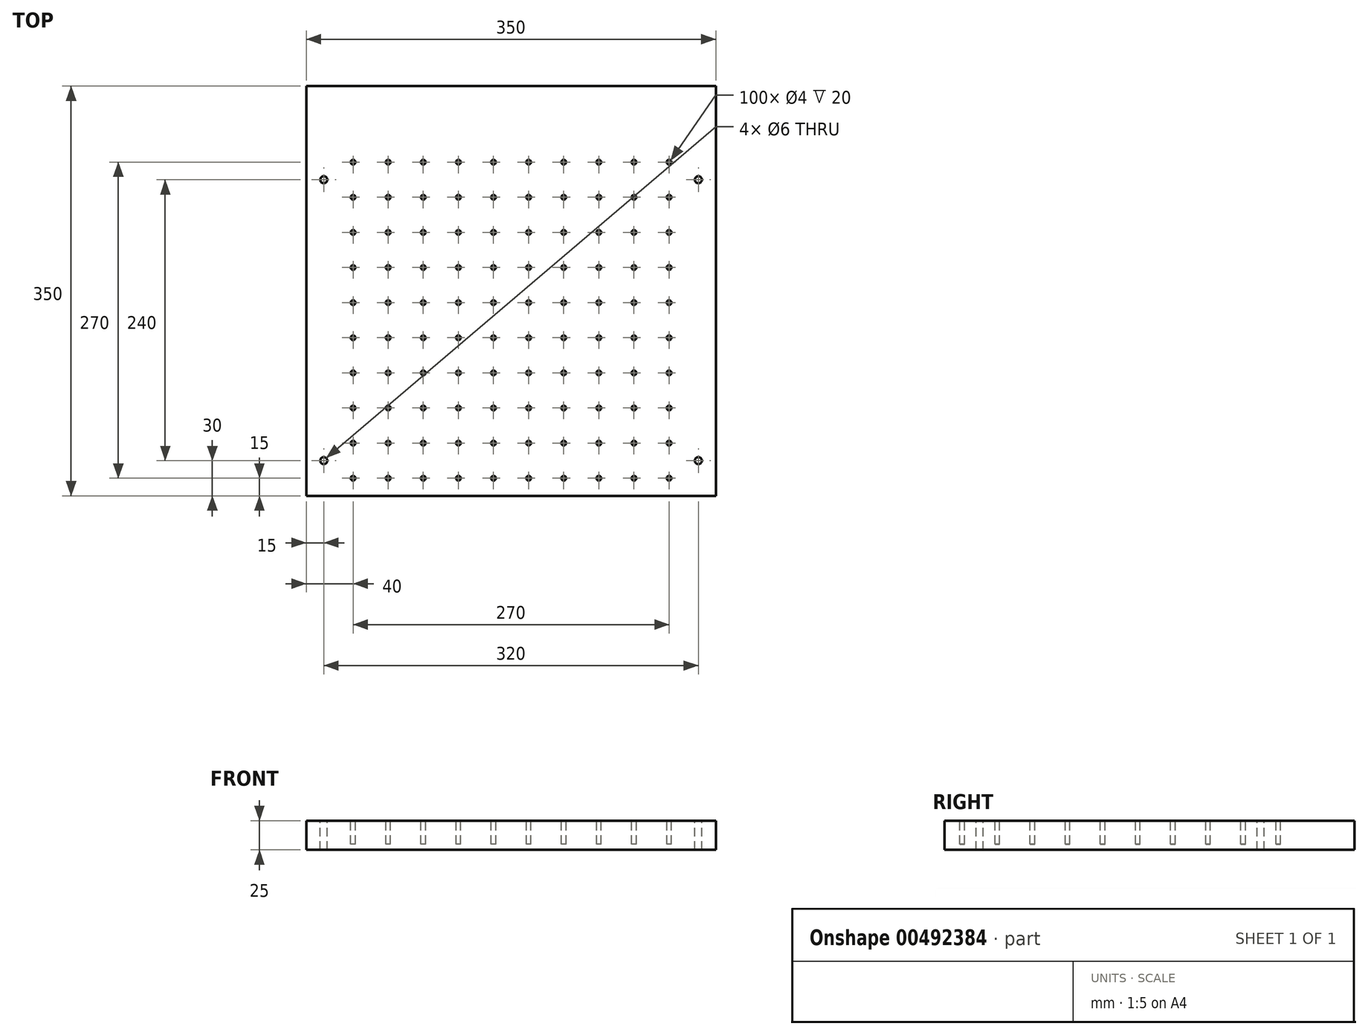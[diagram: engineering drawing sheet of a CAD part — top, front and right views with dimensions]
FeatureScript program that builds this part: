
annotation { "Feature Type Name" : "Feature", "Feature Type Description" : "" }
export const myFeature = defineFeature(function(context is Context, id is Id, definition is map)
    precondition{}
    {
        {
            var Q0;
            Q0=qCreatedBy(makeId("Top.planeOp"),FACE);
            var sketch = newSketch(context, id + "F0", { "sketchPlane" : qUnion([Q0])});
            skLineSegment(sketch, "E0.bottom", {"start": v(0, 0) * mm, "end": v(350, 0) * mm});
            skLineSegment(sketch, "E0.top", {"start": v(0, 300) * mm, "end": v(350, 300) * mm});
            skLineSegment(sketch, "E0.left", {"start": v(0, 0) * mm, "end": v(0, 300) * mm});
            skLineSegment(sketch, "E0.right", {"start": v(350, 0) * mm, "end": v(350, 300) * mm});
            skLineSegment(sketch, "E1.top", {"start": v(0, 350) * mm, "end": v(350, 350) * mm});
            skLineSegment(sketch, "E1.left", {"start": v(0, 300) * mm, "end": v(0, 350) * mm});
            skLineSegment(sketch, "E1.right", {"start": v(350, 300) * mm, "end": v(350, 350) * mm});
            skSolve(sketch);
        }
        {
            var Q0;
            Q0 = qSketchRegion(id + "F0", true);
            extrude(context, id + "F1", {"entities" : qUnion([Q0]), "depth" : 25 * mm});
        }
        {
            var Q0;
            Q0=makeQuery(id+"F1.opExtrude","CAP_FACE",FACE,{"disambiguationData":[OSD([sQuery(id+"F0.wireOp",EDGE,"E0.bottom"),sQuery(id+"F0.wireOp",EDGE,"E0.top"),sQuery(id+"F0.wireOp",EDGE,"E0.left"),sQuery(id+"F0.wireOp",EDGE,"E0.right")])],"isStart":false});
            var sketch = newSketch(context, id + "F2", { "sketchPlane" : qUnion([Q0])});
            skCircle(sketch, "E2", {"center": v(40, 15) * mm, "radius": 2 * mm});
            skCircle(sketch, "E3.0.1.0", {"center": v(40, 45) * mm, "radius": 2 * mm});
            skCircle(sketch, "E3.0.2.0", {"center": v(40, 75) * mm, "radius": 2 * mm});
            skCircle(sketch, "E3.0.3.0", {"center": v(40, 105) * mm, "radius": 2 * mm});
            skCircle(sketch, "E3.0.4.0", {"center": v(40, 135) * mm, "radius": 2 * mm});
            skCircle(sketch, "E3.0.5.0", {"center": v(40, 165) * mm, "radius": 2 * mm});
            skCircle(sketch, "E3.0.6.0", {"center": v(40, 195) * mm, "radius": 2 * mm});
            skCircle(sketch, "E3.0.7.0", {"center": v(40, 225) * mm, "radius": 2 * mm});
            skCircle(sketch, "E3.0.8.0", {"center": v(40, 255) * mm, "radius": 2 * mm});
            skCircle(sketch, "E3.0.9.0", {"center": v(40, 285) * mm, "radius": 2 * mm});
            skCircle(sketch, "E3.1.0.0", {"center": v(70, 15) * mm, "radius": 2 * mm});
            skCircle(sketch, "E3.1.1.0", {"center": v(70, 45) * mm, "radius": 2 * mm});
            skCircle(sketch, "E3.1.2.0", {"center": v(70, 75) * mm, "radius": 2 * mm});
            skCircle(sketch, "E3.1.3.0", {"center": v(70, 105) * mm, "radius": 2 * mm});
            skCircle(sketch, "E3.1.4.0", {"center": v(70, 135) * mm, "radius": 2 * mm});
            skCircle(sketch, "E3.1.5.0", {"center": v(70, 165) * mm, "radius": 2 * mm});
            skCircle(sketch, "E3.1.6.0", {"center": v(70, 195) * mm, "radius": 2 * mm});
            skCircle(sketch, "E3.1.7.0", {"center": v(70, 225) * mm, "radius": 2 * mm});
            skCircle(sketch, "E3.1.8.0", {"center": v(70, 255) * mm, "radius": 2 * mm});
            skCircle(sketch, "E3.1.9.0", {"center": v(70, 285) * mm, "radius": 2 * mm});
            skCircle(sketch, "E3.2.0.0", {"center": v(100, 15) * mm, "radius": 2 * mm});
            skCircle(sketch, "E3.2.1.0", {"center": v(100, 45) * mm, "radius": 2 * mm});
            skCircle(sketch, "E3.2.2.0", {"center": v(100, 75) * mm, "radius": 2 * mm});
            skCircle(sketch, "E3.2.3.0", {"center": v(100, 105) * mm, "radius": 2 * mm});
            skCircle(sketch, "E3.2.4.0", {"center": v(100, 135) * mm, "radius": 2 * mm});
            skCircle(sketch, "E3.2.5.0", {"center": v(100, 165) * mm, "radius": 2 * mm});
            skCircle(sketch, "E3.2.6.0", {"center": v(100, 195) * mm, "radius": 2 * mm});
            skCircle(sketch, "E3.2.7.0", {"center": v(100, 225) * mm, "radius": 2 * mm});
            skCircle(sketch, "E3.2.8.0", {"center": v(100, 255) * mm, "radius": 2 * mm});
            skCircle(sketch, "E3.2.9.0", {"center": v(100, 285) * mm, "radius": 2 * mm});
            skCircle(sketch, "E3.3.0.0", {"center": v(130, 15) * mm, "radius": 2 * mm});
            skCircle(sketch, "E3.3.1.0", {"center": v(130, 45) * mm, "radius": 2 * mm});
            skCircle(sketch, "E3.3.2.0", {"center": v(130, 75) * mm, "radius": 2 * mm});
            skCircle(sketch, "E3.3.3.0", {"center": v(130, 105) * mm, "radius": 2 * mm});
            skCircle(sketch, "E3.3.4.0", {"center": v(130, 135) * mm, "radius": 2 * mm});
            skCircle(sketch, "E3.3.5.0", {"center": v(130, 165) * mm, "radius": 2 * mm});
            skCircle(sketch, "E3.3.6.0", {"center": v(130, 195) * mm, "radius": 2 * mm});
            skCircle(sketch, "E3.3.7.0", {"center": v(130, 225) * mm, "radius": 2 * mm});
            skCircle(sketch, "E3.3.8.0", {"center": v(130, 255) * mm, "radius": 2 * mm});
            skCircle(sketch, "E3.3.9.0", {"center": v(130, 285) * mm, "radius": 2 * mm});
            skCircle(sketch, "E3.4.0.0", {"center": v(160, 15) * mm, "radius": 2 * mm});
            skCircle(sketch, "E3.4.1.0", {"center": v(160, 45) * mm, "radius": 2 * mm});
            skCircle(sketch, "E3.4.2.0", {"center": v(160, 75) * mm, "radius": 2 * mm});
            skCircle(sketch, "E3.4.3.0", {"center": v(160, 105) * mm, "radius": 2 * mm});
            skCircle(sketch, "E3.4.4.0", {"center": v(160, 135) * mm, "radius": 2 * mm});
            skCircle(sketch, "E3.4.5.0", {"center": v(160, 165) * mm, "radius": 2 * mm});
            skCircle(sketch, "E3.4.6.0", {"center": v(160, 195) * mm, "radius": 2 * mm});
            skCircle(sketch, "E3.4.7.0", {"center": v(160, 225) * mm, "radius": 2 * mm});
            skCircle(sketch, "E3.4.8.0", {"center": v(160, 255) * mm, "radius": 2 * mm});
            skCircle(sketch, "E3.4.9.0", {"center": v(160, 285) * mm, "radius": 2 * mm});
            skCircle(sketch, "E3.5.0.0", {"center": v(190, 15) * mm, "radius": 2 * mm});
            skCircle(sketch, "E3.5.1.0", {"center": v(190, 45) * mm, "radius": 2 * mm});
            skCircle(sketch, "E3.5.2.0", {"center": v(190, 75) * mm, "radius": 2 * mm});
            skCircle(sketch, "E3.5.3.0", {"center": v(190, 105) * mm, "radius": 2 * mm});
            skCircle(sketch, "E3.5.4.0", {"center": v(190, 135) * mm, "radius": 2 * mm});
            skCircle(sketch, "E3.5.5.0", {"center": v(190, 165) * mm, "radius": 2 * mm});
            skCircle(sketch, "E3.5.6.0", {"center": v(190, 195) * mm, "radius": 2 * mm});
            skCircle(sketch, "E3.5.7.0", {"center": v(190, 225) * mm, "radius": 2 * mm});
            skCircle(sketch, "E3.5.8.0", {"center": v(190, 255) * mm, "radius": 2 * mm});
            skCircle(sketch, "E3.5.9.0", {"center": v(190, 285) * mm, "radius": 2 * mm});
            skCircle(sketch, "E3.6.0.0", {"center": v(220, 15) * mm, "radius": 2 * mm});
            skCircle(sketch, "E3.6.1.0", {"center": v(220, 45) * mm, "radius": 2 * mm});
            skCircle(sketch, "E3.6.2.0", {"center": v(220, 75) * mm, "radius": 2 * mm});
            skCircle(sketch, "E3.6.3.0", {"center": v(220, 105) * mm, "radius": 2 * mm});
            skCircle(sketch, "E3.6.4.0", {"center": v(220, 135) * mm, "radius": 2 * mm});
            skCircle(sketch, "E3.6.5.0", {"center": v(220, 165) * mm, "radius": 2 * mm});
            skCircle(sketch, "E3.6.6.0", {"center": v(220, 195) * mm, "radius": 2 * mm});
            skCircle(sketch, "E3.6.7.0", {"center": v(220, 225) * mm, "radius": 2 * mm});
            skCircle(sketch, "E3.6.8.0", {"center": v(220, 255) * mm, "radius": 2 * mm});
            skCircle(sketch, "E3.6.9.0", {"center": v(220, 285) * mm, "radius": 2 * mm});
            skCircle(sketch, "E3.7.0.0", {"center": v(250, 15) * mm, "radius": 2 * mm});
            skCircle(sketch, "E3.7.1.0", {"center": v(250, 45) * mm, "radius": 2 * mm});
            skCircle(sketch, "E3.7.2.0", {"center": v(250, 75) * mm, "radius": 2 * mm});
            skCircle(sketch, "E3.7.3.0", {"center": v(250, 105) * mm, "radius": 2 * mm});
            skCircle(sketch, "E3.7.4.0", {"center": v(250, 135) * mm, "radius": 2 * mm});
            skCircle(sketch, "E3.7.5.0", {"center": v(250, 165) * mm, "radius": 2 * mm});
            skCircle(sketch, "E3.7.6.0", {"center": v(250, 195) * mm, "radius": 2 * mm});
            skCircle(sketch, "E3.7.7.0", {"center": v(250, 225) * mm, "radius": 2 * mm});
            skCircle(sketch, "E3.7.8.0", {"center": v(250, 255) * mm, "radius": 2 * mm});
            skCircle(sketch, "E3.7.9.0", {"center": v(250, 285) * mm, "radius": 2 * mm});
            skCircle(sketch, "E3.8.0.0", {"center": v(280, 15) * mm, "radius": 2 * mm});
            skCircle(sketch, "E3.8.1.0", {"center": v(280, 45) * mm, "radius": 2 * mm});
            skCircle(sketch, "E3.8.2.0", {"center": v(280, 75) * mm, "radius": 2 * mm});
            skCircle(sketch, "E3.8.3.0", {"center": v(280, 105) * mm, "radius": 2 * mm});
            skCircle(sketch, "E3.8.4.0", {"center": v(280, 135) * mm, "radius": 2 * mm});
            skCircle(sketch, "E3.8.5.0", {"center": v(280, 165) * mm, "radius": 2 * mm});
            skCircle(sketch, "E3.8.6.0", {"center": v(280, 195) * mm, "radius": 2 * mm});
            skCircle(sketch, "E3.8.7.0", {"center": v(280, 225) * mm, "radius": 2 * mm});
            skCircle(sketch, "E3.8.8.0", {"center": v(280, 255) * mm, "radius": 2 * mm});
            skCircle(sketch, "E3.8.9.0", {"center": v(280, 285) * mm, "radius": 2 * mm});
            skCircle(sketch, "E3.9.0.0", {"center": v(310, 15) * mm, "radius": 2 * mm});
            skCircle(sketch, "E3.9.1.0", {"center": v(310, 45) * mm, "radius": 2 * mm});
            skCircle(sketch, "E3.9.2.0", {"center": v(310, 75) * mm, "radius": 2 * mm});
            skCircle(sketch, "E3.9.3.0", {"center": v(310, 105) * mm, "radius": 2 * mm});
            skCircle(sketch, "E3.9.4.0", {"center": v(310, 135) * mm, "radius": 2 * mm});
            skCircle(sketch, "E3.9.5.0", {"center": v(310, 165) * mm, "radius": 2 * mm});
            skCircle(sketch, "E3.9.6.0", {"center": v(310, 195) * mm, "radius": 2 * mm});
            skCircle(sketch, "E3.9.7.0", {"center": v(310, 225) * mm, "radius": 2 * mm});
            skCircle(sketch, "E3.9.8.0", {"center": v(310, 255) * mm, "radius": 2 * mm});
            skCircle(sketch, "E3.9.9.0", {"center": v(310, 285) * mm, "radius": 2 * mm});
            skLineSegment(sketch, "E3.direction1", {"start": v(40, 15) * mm, "end": v(70, 15) * mm, "construction": true});
            skLineSegment(sketch, "E3.direction2", {"start": v(40, 15) * mm, "end": v(40, 45) * mm, "construction": true});
            skSolve(sketch);
        }
        {
            var Q0;
            Q0 = qSketchRegion(id + "F2", true);
            extrude(context, id + "F3", {"entities" : qUnion([Q0]), "operationType" : NewBodyOperationType.REMOVE, "oppositeDirection" : true, "depth" : 20 * mm});
        }
        {
            var Q0;
            Q0=makeQuery(id+"F1.opExtrude","CAP_FACE",FACE,{"disambiguationData":[OSD([sQuery(id+"F0.wireOp",EDGE,"E0.bottom"),sQuery(id+"F0.wireOp",EDGE,"E0.left"),sQuery(id+"F0.wireOp",EDGE,"E0.right"),sQuery(id+"F0.wireOp",EDGE,"E1.top"),sQuery(id+"F0.wireOp",EDGE,"E1.left"),sQuery(id+"F0.wireOp",EDGE,"E1.right")])],"isStart":false});
            var sketch = newSketch(context, id + "F4", { "sketchPlane" : qUnion([Q0])});
            skCircle(sketch, "E4", {"center": v(15, 270) * mm, "radius": 3 * mm});
            skCircle(sketch, "E5", {"center": v(335, 270) * mm, "radius": 3 * mm});
            skCircle(sketch, "E6", {"center": v(335, 30) * mm, "radius": 3 * mm});
            skCircle(sketch, "E7", {"center": v(15, 30) * mm, "radius": 3 * mm});
            skSolve(sketch);
        }
        {
            var Q0;
            Q0 = qSketchRegion(id + "F4", true);
            extrude(context, id + "F5", {"entities" : qUnion([Q0]), "operationType" : NewBodyOperationType.REMOVE, "endBound" : BoundingType.THROUGH_ALL, "oppositeDirection" : true, "depth" : 25 * mm});
        }
    });
